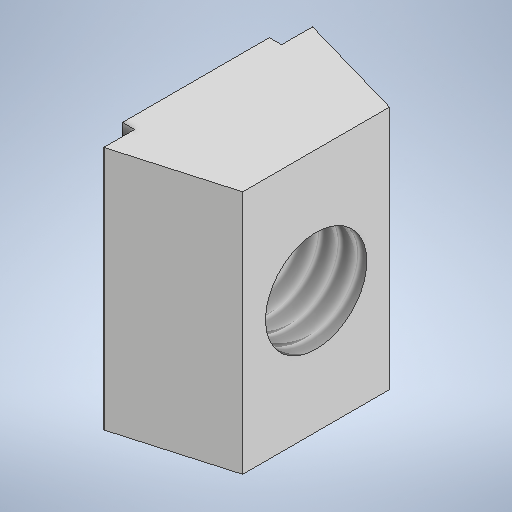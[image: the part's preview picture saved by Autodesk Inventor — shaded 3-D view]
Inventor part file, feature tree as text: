
AUTODESK INVENTOR PART (.ipt)
format: ipt  version: 2025 (Build 290162000, 162)  size: 221,184 bytes
history: native  units: mm
features: sketch x2, extrude x1, hole x1
ambient origin geometry x8: Origin, YZ Plane, XZ Plane, XY Plane, X Axis, Y Axis, Z Axis, Center Point
bodies: Solid1 (feature_tree)
feature tree (4):
  extrude  "Extrusion1"  Depth=0.5mm
  hole  "Hole2"  [1 undecoded]
  sketch  "Sketch1"  dims[d0=6.0mm d1=0.5mm]
  sketch  "Sketch2"  dims[d4=4.4mm d5=10.0mm d6=0.0mm d14=4.134mm d15=10.0mm d16=4.0mm d17=2.0mm d18=90.0deg d19=8.0mm d20=20.594885mm]
note: 1 required parameter value undecoded (feature->parameter linkage not recoverable at this tier; creation-order binding heuristic only, values carry confidence <= 0.55)
